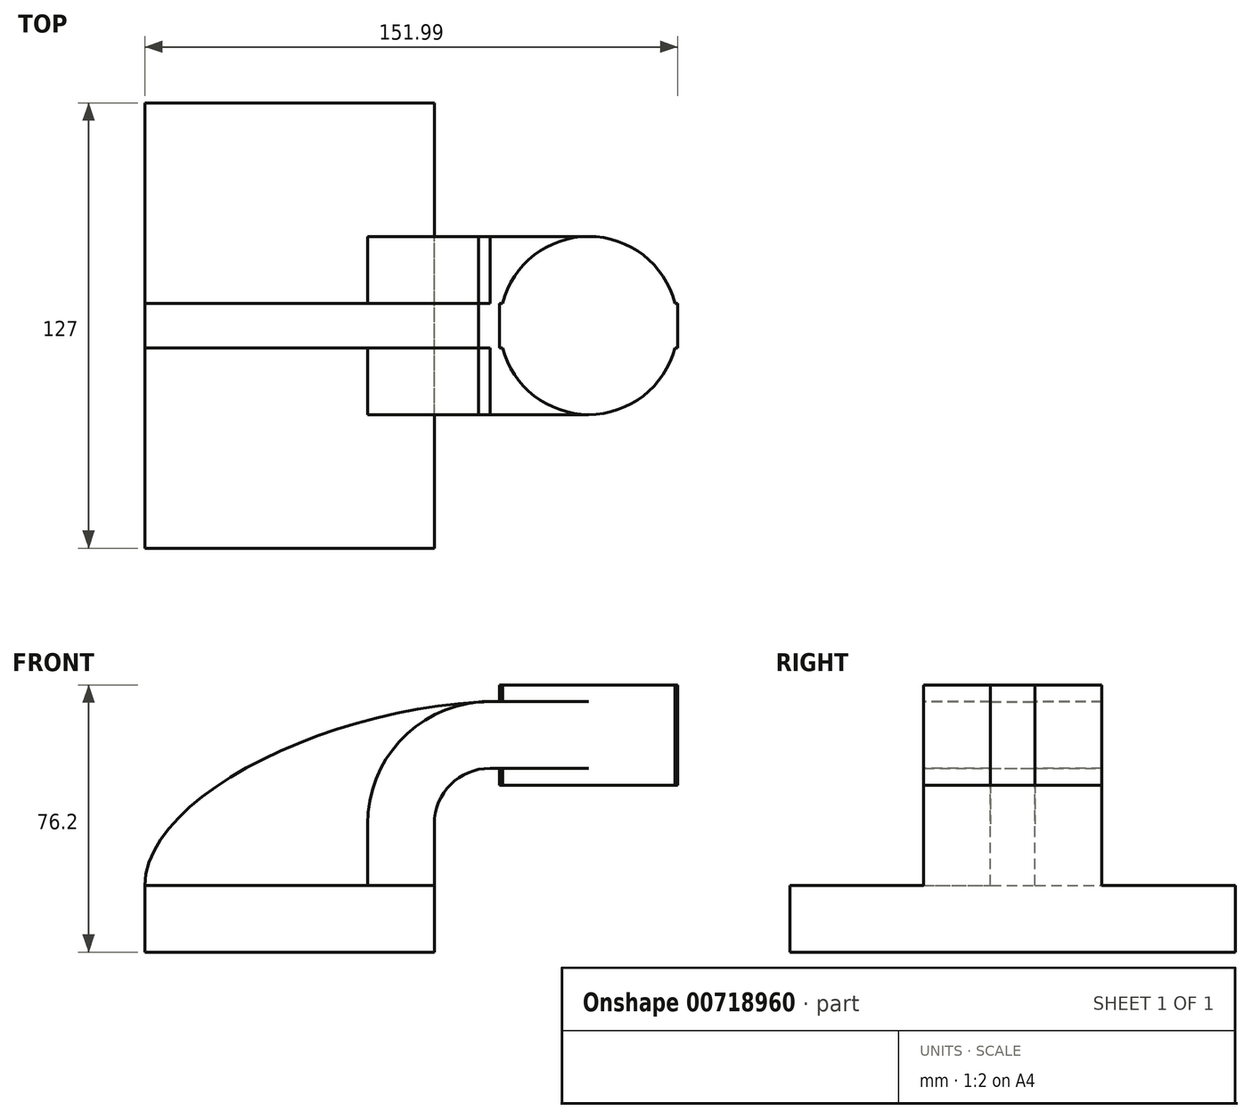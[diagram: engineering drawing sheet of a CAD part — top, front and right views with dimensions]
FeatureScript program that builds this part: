
annotation { "Feature Type Name" : "Feature", "Feature Type Description" : "" }
export const myFeature = defineFeature(function(context is Context, id is Id, definition is map)
    precondition{}
    {
        {
            var Q0;
            Q0=qCreatedBy(makeId("Front.planeOp"),FACE);
            var sketch = newSketch(context, id + "F0", { "sketchPlane" : qUnion([Q0])});
            skLineSegment(sketch, "E0.bottom", {"start": v(-41.28, 9.52) * mm, "end": v(41.28, 9.53) * mm});
            skLineSegment(sketch, "E0.top", {"start": v(-41.28, -9.52) * mm, "end": v(41.28, -9.52) * mm});
            skLineSegment(sketch, "E0.left", {"start": v(-41.28, 9.52) * mm, "end": v(-41.27, -9.53) * mm});
            skLineSegment(sketch, "E0.right", {"start": v(41.28, 9.53) * mm, "end": v(41.28, -9.52) * mm});
            skPoint(sketch, "E0.middle", {"position": v(0, 0) * mm});
            skLineSegment(sketch, "E1.bottom", {"start": v(59.9, 38.1) * mm, "end": v(110.7, 38.1) * mm});
            skLineSegment(sketch, "E1.top", {"start": v(59.9, 66.68) * mm, "end": v(110.7, 66.68) * mm});
            skLineSegment(sketch, "E1.left", {"start": v(59.9, 38.1) * mm, "end": v(59.9, 66.67) * mm});
            skLineSegment(sketch, "E1.right", {"start": v(110.7, 38.1) * mm, "end": v(110.7, 66.68) * mm});
            skPoint(sketch, "E1.middle", {"position": v(85.3, 52.39) * mm});
            skLineSegment(sketch, "E2", {"start": v(41.27, 9.53) * mm, "end": v(41.27, 27) * mm});
            skArc(sketch, "E3", {"start": v(41.27, 27) * mm, "mid": v(45.92, 38.23) * mm, "end": v(57.15, 42.88) * mm});
            skLineSegment(sketch, "E4", {"start": v(57.15, 42.88) * mm, "end": v(85.3, 42.88) * mm});
            skLineSegment(sketch, "E5.0", {"start": v(57.15, 61.93) * mm, "end": v(85.3, 61.93) * mm});
            skArc(sketch, "E5.1", {"start": v(22.22, 27) * mm, "mid": v(32.45, 51.7) * mm, "end": v(57.15, 61.93) * mm});
            skLineSegment(sketch, "E5.2", {"start": v(22.22, 9.53) * mm, "end": v(22.22, 27) * mm});
            skLineSegment(sketch, "E6", {"start": v(85.3, 38.1) * mm, "end": v(85.3, 66.67) * mm});
            skFitSpline(sketch, "E7", {"points": [v(-41.28, 9.52) * mm, v(57.15, 61.93) * mm], "startDerivative": vector(1.72, 78.02) * mm, "endDerivative": vector(134.52, 4.56) * mm});
            skSolve(sketch);
        }
        {
            var Q0;
            Q0=makeQuery(id+"F0.imprint","IMPRINT",FACE,{"disambiguationData":[TD([[makeQuery(id+"F0.imprint","IMPRINT",EDGE,{"derivedFrom":sQuery(id+"F0.wireOp",EDGE,"E0.top")}),1.0]])]});
            extrude(context, id + "F1", {"entities" : qUnion([Q0]), "endBound" : BoundingType.SYMMETRIC, "depth" : 127 * mm, "offsetDistance" : 25.4 * mm});
        }
        {
            var Q0;
            {var subQ1=sQuery(id+"F0.wireOp",EDGE,"E2");Q0=makeQuery(id+"F0.imprint","IMPRINT",FACE,{"disambiguationData":[TD([[makeQuery(id+"F0.imprint","IMPRINT",EDGE,{"derivedFrom":subQ1}),1.0]])]});}
            var Q1;
            {var subQ0=sQuery(id+"F0.wireOp",EDGE,"E4");var subQ1=sQuery(id+"F0.wireOp",EDGE,"E1.left");var subQ2=makeQuery(id+"F0.imprint","INTERSECT",VERTEX,{"derivedFrom":[subQ1,subQ0]});Q1=makeQuery(id+"F0.imprint","IMPRINT",FACE,{"disambiguationData":[TD([[makeQuery(id+"F0.imprint","IMPRINT",EDGE,{"disambiguationData":[TD([[subQ2,-1.0]])],"derivedFrom":subQ1}),-1.0]])]});}
            extrude(context, id + "F2", {"entities" : qUnion([Q0, Q1]), "operationType" : NewBodyOperationType.ADD, "endBound" : BoundingType.SYMMETRIC, "depth" : 50.8 * mm, "offsetDistance" : 25.4 * mm});
        }
        {
            var Q0;
            Q0 = qSketchRegion(id + "F0", true);
            extrude(context, id + "F3", {"entities" : qUnion([Q0]), "operationType" : NewBodyOperationType.ADD, "endBound" : BoundingType.SYMMETRIC, "depth" : 12.7 * mm, "offsetDistance" : 25.4 * mm});
        }
        {
            var Q0;
            {var subQ4=sQuery(id+"F0.wireOp",EDGE,"E1.right");Q0=makeQuery(id+"F0.imprint","IMPRINT",FACE,{"disambiguationData":[TD([[makeQuery(id+"F0.imprint","IMPRINT",EDGE,{"derivedFrom":subQ4}),1.0]])]});}
            var Q1;
            Q1=sQuery(id+"F0.wireOp",EDGE,"E6");
            revolve(context, id + "F4", {"operationType" : NewBodyOperationType.ADD, "surfaceOperationType" : NewSurfaceOperationType.NEW, "entities" : qUnion([Q0]), "axis" : qUnion([Q1]), "revolveType" : RevolveType.FULL});
        }
    });
